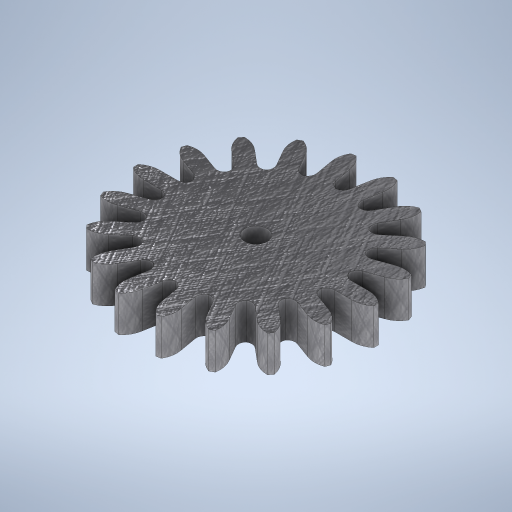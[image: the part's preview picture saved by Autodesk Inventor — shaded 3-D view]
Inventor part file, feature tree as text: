
AUTODESK INVENTOR PART (.ipt)
format: ipt  version: 2024 (Build 280153020, 153B)  size: 610,304 bytes
history: native  units: mm
features: extrude x1, sketch x1
ambient origin geometry x8: Origin, YZ Plane, XZ Plane, XY Plane, X Axis, Y Axis, Z Axis, Center Point
bodies: Solid1 (feature_tree)
feature tree (2):
  extrude  "Extrusion1"  Depth=4.5mm
  sketch  "Sketch1"  dims[d0=2.8mm d1=20.0mm d4=1.570796mm d5=0.785398mm d6=3.0mm d7=0.3mm d8=0.6mm d9=3.0mm d11=1.0mm d12=1.0mm d13=180.0mm d15=360.0deg d17=4.5mm d18=0.0mm d19=20.0mm]
